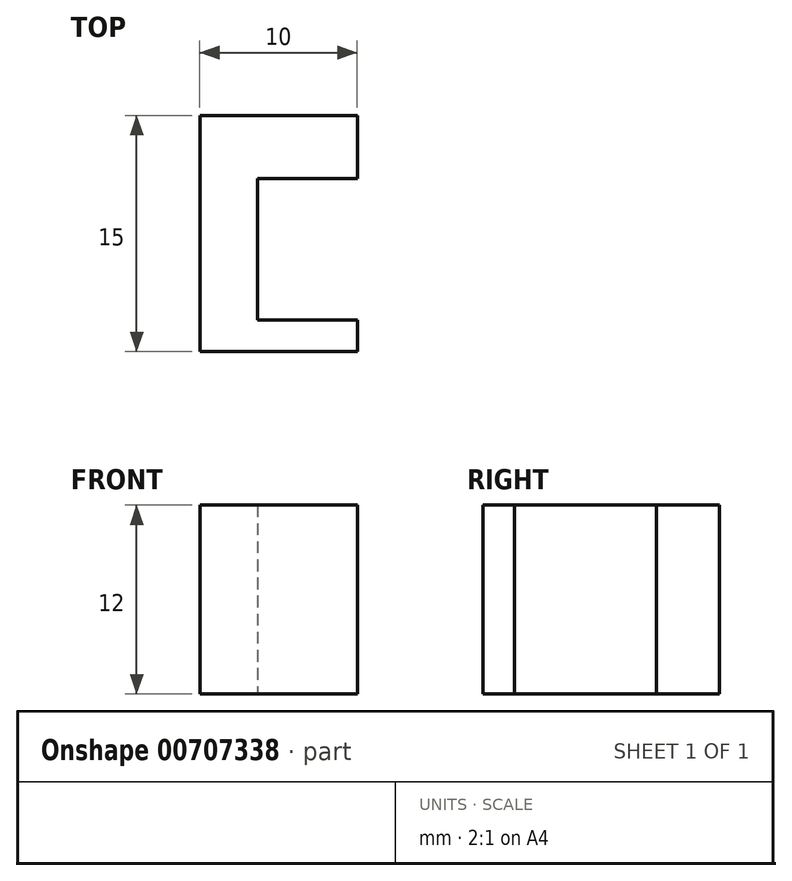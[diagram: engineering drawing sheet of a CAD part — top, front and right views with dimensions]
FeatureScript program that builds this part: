
annotation { "Feature Type Name" : "Feature", "Feature Type Description" : "" }
export const myFeature = defineFeature(function(context is Context, id is Id, definition is map)
    precondition{}
    {
        {
            var Q0;
            Q0=qCreatedBy(makeId("Top.planeOp"),FACE);
            var sketch = newSketch(context, id + "F0", { "sketchPlane" : qUnion([Q0])});
            skLineSegment(sketch, "E0.bottom", {"start": v(-26.8, 12.35) * mm, "end": v(-16.8, 12.35) * mm});
            skLineSegment(sketch, "E0.top", {"start": v(-26.8, -2.65) * mm, "end": v(-16.8, -2.65) * mm});
            skLineSegment(sketch, "E0.left", {"start": v(-26.8, 12.35) * mm, "end": v(-26.8, -2.65) * mm});
            skLineSegment(sketch, "E0.right", {"start": v(-16.8, 12.35) * mm, "end": v(-16.8, -2.65) * mm});
            skLineSegment(sketch, "E1.bottom", {"start": v(-16.8, 8.35) * mm, "end": v(-23.13, 8.35) * mm});
            skLineSegment(sketch, "E1.top", {"start": v(-16.8, -0.65) * mm, "end": v(-23.13, -0.65) * mm});
            skLineSegment(sketch, "E1.left", {"start": v(-16.8, 8.35) * mm, "end": v(-16.8, -0.65) * mm});
            skLineSegment(sketch, "E1.right", {"start": v(-23.13, 8.35) * mm, "end": v(-23.13, -0.65) * mm});
            skSolve(sketch);
        }
        {
            var Q0;
            {var subQ1=sQuery(id+"F0.wireOp",EDGE,"E0.bottom");Q0=makeQuery(id+"F0.imprint","IMPRINT",FACE,{"disambiguationData":[TD([[makeQuery(id+"F0.imprint","IMPRINT",EDGE,{"derivedFrom":subQ1}),-1.0]])]});}
            extrude(context, id + "F1", {"entities" : qUnion([Q0]), "depth" : 12 * mm, "offsetDistance" : 25 * mm});
        }
    });
